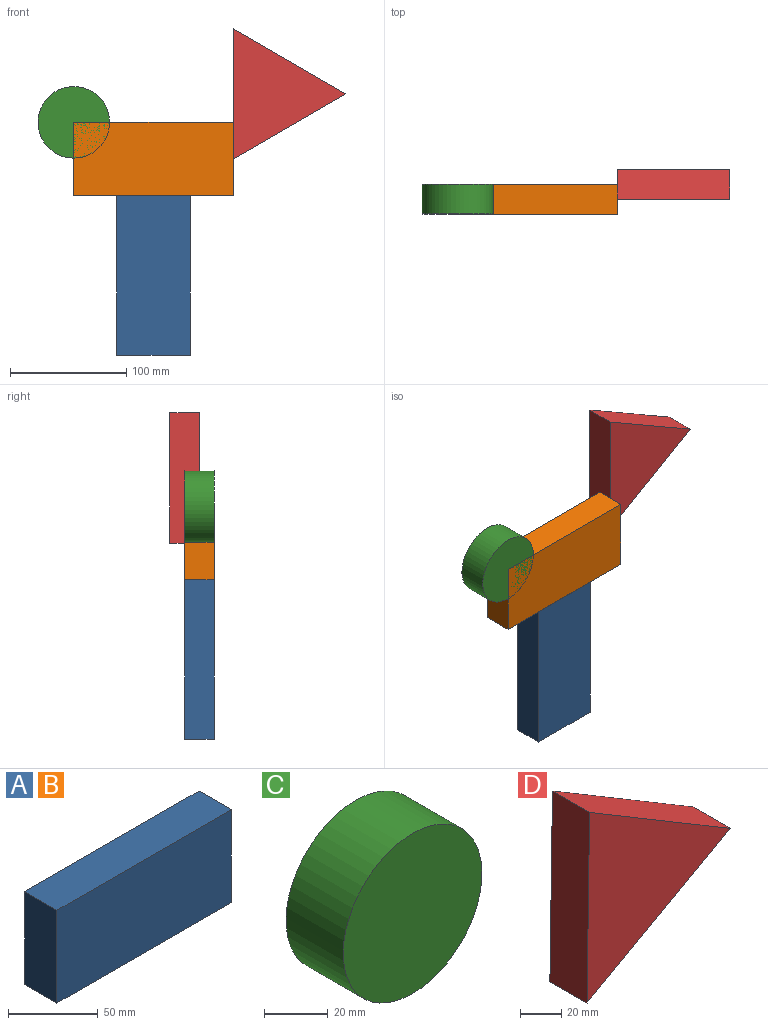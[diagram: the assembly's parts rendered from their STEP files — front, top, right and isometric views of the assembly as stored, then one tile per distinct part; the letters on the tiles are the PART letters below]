
ASSEMBLY  parts=4 mates=3
PART A: 6 faces, bbox 137.2x25.4x63.2 mm
  f0: plane 63.24x25.4mm, normal (1,0,0), area 1606.2mm2, adj f1,f3,f4,f5
  f1: plane 137.21x25.4mm, normal (0,0,1), area 3485.2mm2, adj f0,f2,f4,f5
  f2: plane 63.24x25.4mm, normal (-1,0,0), area 1606.2mm2, adj f1,f3,f4,f5
  f3: plane 137.21x25.4mm, normal (0,0,-1), area 3485.2mm2, adj f0,f2,f4,f5
  f4: plane 137.21x63.24mm, normal (0,-1,0), area 8676.9mm2, adj f0,f1,f2,f3
  f5: plane 137.21x63.24mm, normal (0,1,0), area 8676.9mm2, adj f0,f1,f2,f3
PART B: same geometry as A
PART C: 3 faces, bbox 61.6x25.4x61.6 mm
  f0: cylinder r=30.82mm len=61.64mm, axis (0,1,0), area 4918.9mm2, adj f1,f2
  f1: plane 61.64x61.64mm, normal (0,-1,0), area 2984.4mm2, adj f0
  f2: plane 61.64x61.64mm, normal (0,1,0), area 2984.4mm2, adj f0
PART D: 5 faces, bbox 98x25.4x112.1 mm
  f0: plane 97.95x54.52mm, normal (0.49,0,-0.87), area 2847.4mm2, adj f1,f2,f3,f4
  f1: plane 96.19x57.57mm, normal (0.51,0,0.86), area 2847.4mm2, adj f0,f2,f3,f4
  f2: plane 112.09x25.4mm, normal (-1,0,0.02), area 2847.4mm2, adj f0,f1,f3,f4
  f3: plane 112.09x97.95mm, normal (0,-1,0), area 5441.6mm2, adj f0,f1,f2
  f4: plane 112.09x97.95mm, normal (0,1,0), area 5441.6mm2, adj f0,f1,f2
PLACE A rot(axis=(0,-1,0),90deg) t=(0,25.4,-100.23)mm
PLACE B t=(0,25.4,0)mm
PLACE C t=(47.43,25.4,31.62)mm
PLACE D rot(axis=(0,-1,0),0.9deg) t=(-44.03,38.1,53.77)mm
MATE fastened D.f2 <-> B.f0  axis (-1,0,0) through (68.61,25.4,0)mm
MATE fastened A.f0 <-> B.f3  axis (0,0,1) through (0,12.7,-31.62)mm
MATE fastened C.f0 <-> B.f4  axis (0,-1,0) through (-68.61,0,31.62)mm
